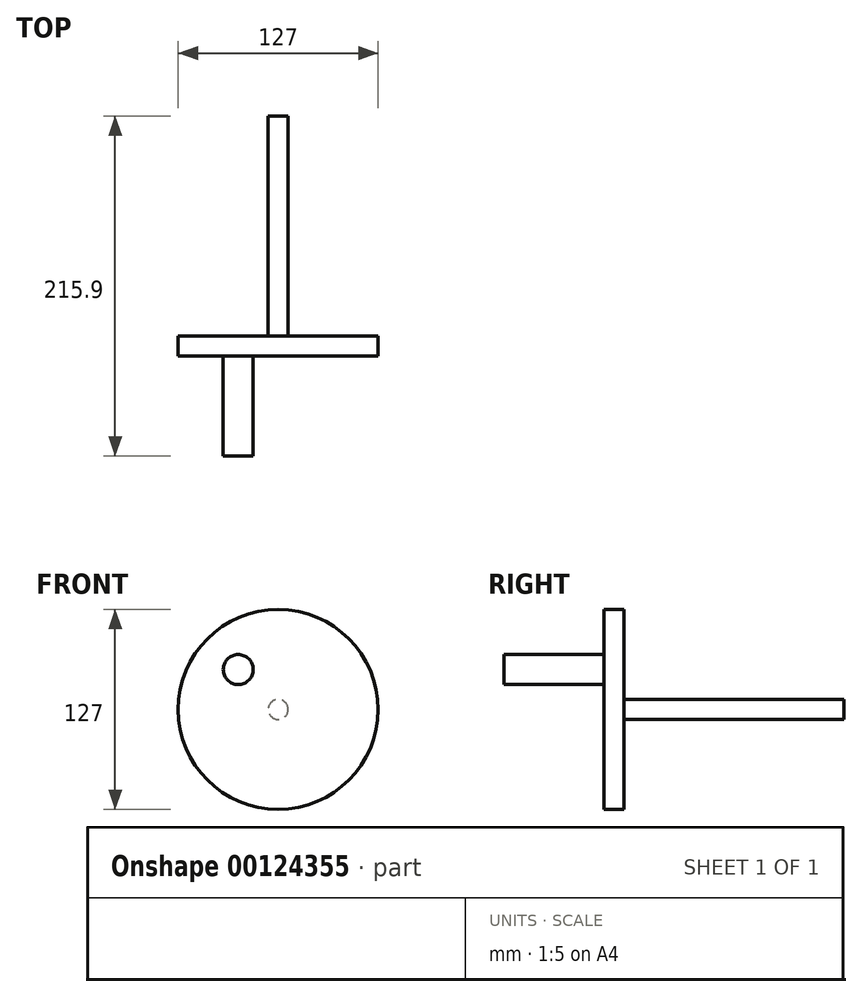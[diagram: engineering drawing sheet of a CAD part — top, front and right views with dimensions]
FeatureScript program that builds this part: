
annotation { "Feature Type Name" : "Feature", "Feature Type Description" : "" }
export const myFeature = defineFeature(function(context is Context, id is Id, definition is map)
    precondition{}
    {
        {
            var Q0;
            Q0=qCreatedBy(makeId("Front.planeOp"),FACE);
            var sketch = newSketch(context, id + "F0", { "sketchPlane" : qUnion([Q0])});
            skCircle(sketch, "E0", {"center": v(0, 0) * mm, "radius": 63.5 * mm});
            skSolve(sketch);
        }
        {
            var Q0;
            Q0=makeQuery(id+"F0.imprint","IMPRINT",FACE,{"disambiguationData":[TD([[makeQuery(id+"F0.imprint","IMPRINT",EDGE,{"derivedFrom":sQuery(id+"F0.wireOp",EDGE,"E0")}),1.0]])]});
            var sketch = newSketch(context, id + "F1", { "sketchPlane" : qUnion([Q0])});
            skCircle(sketch, "E1", {"center": v(-25.35, 25.35) * mm, "radius": 9.53 * mm});
            skSolve(sketch);
        }
        {
            var Q0;
            Q0=makeQuery(id+"F0.imprint","IMPRINT",FACE,{"disambiguationData":[TD([[makeQuery(id+"F0.imprint","IMPRINT",EDGE,{"derivedFrom":sQuery(id+"F0.wireOp",EDGE,"E0")}),1.0]])]});
            extrude(context, id + "F2", {"entities" : qUnion([Q0]), "depth" : 12.7 * mm});
        }
        {
            var Q0;
            Q0 = qSketchRegion(id + "F1", true);
            extrude(context, id + "F3", {"entities" : qUnion([Q0]), "operationType" : NewBodyOperationType.ADD, "depth" : 76.2 * mm});
        }
        {
            var Q0;
            Q0=qCreatedBy(makeId("Front.planeOp"),FACE);
            var sketch = newSketch(context, id + "F4", { "sketchPlane" : qUnion([Q0])});
            skCircle(sketch, "E2", {"center": v(0, 0) * mm, "radius": 6.35 * mm});
            skSolve(sketch);
        }
        {
            var Q0;
            Q0 = qSketchRegion(id + "F4", true);
            extrude(context, id + "F5", {"entities" : qUnion([Q0]), "operationType" : NewBodyOperationType.ADD, "oppositeDirection" : true, "depth" : 139.7 * mm});
        }
    });
